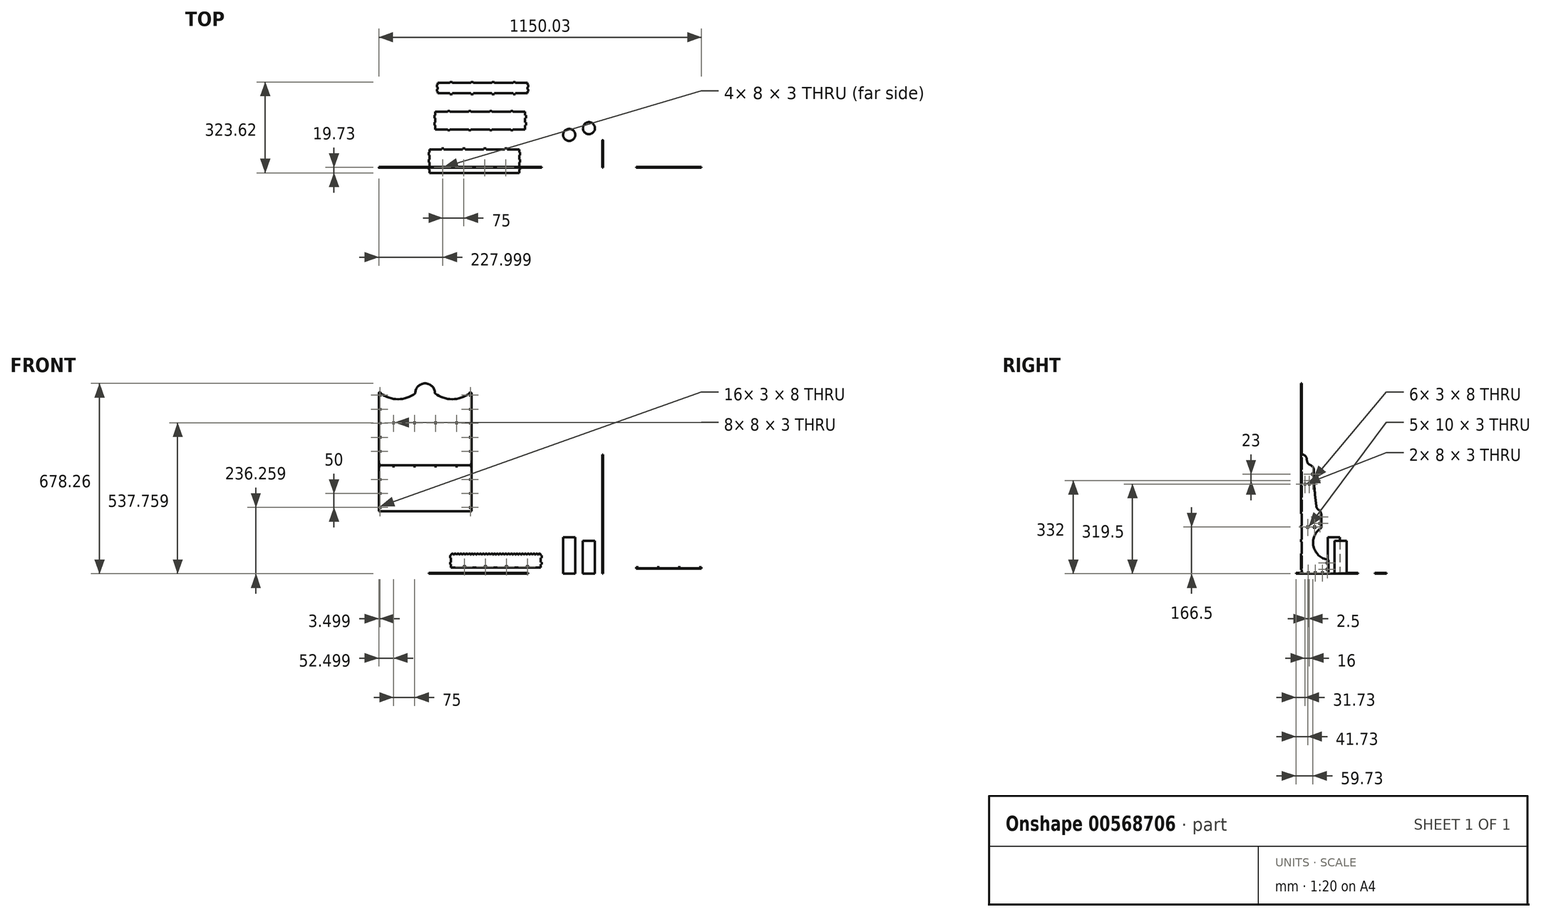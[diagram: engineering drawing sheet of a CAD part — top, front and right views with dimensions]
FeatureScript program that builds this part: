
annotation { "Feature Type Name" : "Feature", "Feature Type Description" : "" }
export const myFeature = defineFeature(function(context is Context, id is Id, definition is map)
    precondition{}
    {
        {
            var Q0;
            Q0=qCreatedBy(makeId("Right.planeOp"),FACE);
            var sketch = newSketch(context, id + "F0", { "sketchPlane" : qUnion([Q0])});
            skLineSegment(sketch, "E0", {"start": v(0, 5) * mm, "end": v(0, 14) * mm});
            skLineSegment(sketch, "E1", {"start": v(5, 0) * mm, "end": v(95, 0) * mm});
            skLineSegment(sketch, "E2", {"start": v(43, 355.36) * mm, "end": v(43, 369.6) * mm});
            skPoint(sketch, "E3", {"position": v(43, 366) * mm});
            skArc(sketch, "E4", {"start": v(5, 0) * mm, "mid": v(3.54, 3.54) * mm, "end": v(0, 5) * mm});
            skLineSegment(sketch, "E5", {"start": v(30.5, 318) * mm, "end": v(22.5, 318) * mm});
            skLineSegment(sketch, "E6", {"start": v(30.5, 321) * mm, "end": v(22.5, 321) * mm});
            skLineSegment(sketch, "E7", {"start": v(37, 359) * mm, "end": v(37, 351) * mm});
            skLineSegment(sketch, "E8", {"start": v(40, 359) * mm, "end": v(40, 351) * mm});
            skPoint(sketch, "E9", {"position": v(0, 474) * mm});
            skPoint(sketch, "E10", {"position": v(37, 359) * mm});
            skPoint(sketch, "E11", {"position": v(37, 351) * mm});
            skPoint(sketch, "E12", {"position": v(37, 336) * mm});
            skPoint(sketch, "E13", {"position": v(37, 328) * mm});
            skLineSegment(sketch, "E14", {"start": v(37, 328) * mm, "end": v(40, 328) * mm});
            skLineSegment(sketch, "E15", {"start": v(37, 336) * mm, "end": v(40, 336) * mm});
            skLineSegment(sketch, "E16", {"start": v(37, 351) * mm, "end": v(40, 351) * mm});
            skLineSegment(sketch, "E17", {"start": v(37, 359) * mm, "end": v(40, 359) * mm});
            skArc(sketch, "E18.trimOffspring", {"start": v(43, 369.6) * mm, "mid": v(38.58, 380.98) * mm, "end": v(28.7, 388.14) * mm});
            skPoint(sketch, "E19.visualSharp", {"position": v(21.6, 389.37) * mm});
            skArc(sketch, "E19.filletArc", {"start": v(18.91, 399.73) * mm, "mid": v(22.23, 392.6) * mm, "end": v(28.7, 388.14) * mm});
            skLineSegment(sketch, "E20.trimOffspring", {"start": v(40, 336) * mm, "end": v(40, 328) * mm});
            skLineSegment(sketch, "E21.trimOffspring", {"start": v(37, 336) * mm, "end": v(37, 328) * mm});
            skLineSegment(sketch, "E22.left", {"start": v(6.5, 321) * mm, "end": v(6.5, 318) * mm});
            skLineSegment(sketch, "E22.right", {"start": v(14.5, 321) * mm, "end": v(14.5, 318) * mm});
            skLineSegment(sketch, "E23.left", {"start": v(22.5, 321) * mm, "end": v(22.5, 318) * mm});
            skLineSegment(sketch, "E23.right", {"start": v(30.5, 321) * mm, "end": v(30.5, 318) * mm});
            skLineSegment(sketch, "E24.trimOffspring", {"start": v(14.5, 321) * mm, "end": v(6.5, 321) * mm});
            skLineSegment(sketch, "E25.trimOffspring", {"start": v(14.5, 318) * mm, "end": v(6.5, 318) * mm});
            skLineSegment(sketch, "E26", {"start": v(43, 318) * mm, "end": v(44, 318) * mm});
            skLineSegment(sketch, "E27.bottom", {"start": v(63, 206) * mm, "end": v(66, 206) * mm});
            skLineSegment(sketch, "E27.top", {"start": v(63, 198) * mm, "end": v(66, 198) * mm});
            skLineSegment(sketch, "E27.left", {"start": v(63, 206) * mm, "end": v(63, 198) * mm});
            skLineSegment(sketch, "E27.right", {"start": v(66, 206) * mm, "end": v(66, 198) * mm});
            skLineSegment(sketch, "E28.bottom", {"start": v(63, 183) * mm, "end": v(66, 183) * mm});
            skLineSegment(sketch, "E28.top", {"start": v(63, 175) * mm, "end": v(66, 175) * mm});
            skLineSegment(sketch, "E28.left", {"start": v(63, 183) * mm, "end": v(63, 175) * mm});
            skLineSegment(sketch, "E28.right", {"start": v(66, 183) * mm, "end": v(66, 175) * mm});
            skLineSegment(sketch, "E29.bottom", {"start": v(40.5, 165) * mm, "end": v(40.5, 168) * mm});
            skLineSegment(sketch, "E29.top", {"start": v(50.5, 165) * mm, "end": v(50.5, 168) * mm});
            skLineSegment(sketch, "E29.left", {"start": v(40.5, 165) * mm, "end": v(50.5, 165) * mm});
            skLineSegment(sketch, "E29.right", {"start": v(40.5, 168) * mm, "end": v(50.5, 168) * mm});
            skLineSegment(sketch, "E30.bottom", {"start": v(15.5, 165) * mm, "end": v(15.5, 168) * mm});
            skLineSegment(sketch, "E30.top", {"start": v(25.5, 165) * mm, "end": v(25.5, 168) * mm});
            skLineSegment(sketch, "E30.left", {"start": v(15.5, 165) * mm, "end": v(25.5, 165) * mm});
            skLineSegment(sketch, "E30.right", {"start": v(15.5, 168) * mm, "end": v(25.5, 168) * mm});
            skArc(sketch, "E31", {"start": v(69, 213) * mm, "mid": v(66.39, 220.9) * mm, "end": v(60.51, 226.8) * mm});
            skLineSegment(sketch, "E32", {"start": v(46.98, 280.85) * mm, "end": v(51.17, 241.67) * mm});
            skPoint(sketch, "E33.visualSharp", {"position": v(43, 318) * mm});
            skArc(sketch, "E33.filletArc", {"start": v(43, 355.36) * mm, "mid": v(44, 318.05) * mm, "end": v(46.98, 280.85) * mm});
            skArc(sketch, "E34.filletArc", {"start": v(51.17, 241.67) * mm, "mid": v(54.12, 233.15) * mm, "end": v(60.51, 226.8) * mm});
            skArc(sketch, "E35", {"start": v(17.5, 407.94) * mm, "mid": v(12.22, 420.03) * mm, "end": v(0, 425) * mm});
            skLineSegment(sketch, "E36", {"start": v(18.91, 399.73) * mm, "end": v(17.5, 407.94) * mm});
            skLineSegment(sketch, "E37.trimOffspring", {"start": v(0, 474) * mm, "end": v(0, 481) * mm});
            skLineSegment(sketch, "E38.bottom", {"start": v(89, 43) * mm, "end": v(92, 43) * mm});
            skLineSegment(sketch, "E38.top", {"start": v(89, 35) * mm, "end": v(92, 35) * mm});
            skLineSegment(sketch, "E38.left", {"start": v(89, 43) * mm, "end": v(89, 35) * mm});
            skLineSegment(sketch, "E38.right", {"start": v(92, 43) * mm, "end": v(92, 35) * mm});
            skLineSegment(sketch, "E39.bottom", {"start": v(92, 20) * mm, "end": v(89, 20) * mm});
            skLineSegment(sketch, "E39.top", {"start": v(92, 12) * mm, "end": v(89, 12) * mm});
            skLineSegment(sketch, "E39.left", {"start": v(92, 20) * mm, "end": v(92, 12) * mm});
            skLineSegment(sketch, "E39.right", {"start": v(89, 20) * mm, "end": v(89, 12) * mm});
            skLineSegment(sketch, "E40", {"start": v(0, 14) * mm, "end": v(-3, 14) * mm});
            skLineSegment(sketch, "E41", {"start": v(-3, 14) * mm, "end": v(-3, 22) * mm});
            skLineSegment(sketch, "E42", {"start": v(-3, 22) * mm, "end": v(0, 22) * mm});
            skLineSegment(sketch, "E43.0.1.0", {"start": v(-3, 72) * mm, "end": v(0, 72) * mm});
            skLineSegment(sketch, "E43.0.1.1", {"start": v(-3, 64) * mm, "end": v(-3, 72) * mm});
            skLineSegment(sketch, "E43.0.1.2", {"start": v(0, 64) * mm, "end": v(-3, 64) * mm});
            skLineSegment(sketch, "E43.0.2.0", {"start": v(-3, 122) * mm, "end": v(0, 122) * mm});
            skLineSegment(sketch, "E43.0.2.1", {"start": v(-3, 114) * mm, "end": v(-3, 122) * mm});
            skLineSegment(sketch, "E43.0.2.2", {"start": v(0, 114) * mm, "end": v(-3, 114) * mm});
            skLineSegment(sketch, "E43.0.3.0", {"start": v(-3, 172) * mm, "end": v(0, 172) * mm});
            skLineSegment(sketch, "E43.0.3.1", {"start": v(-3, 164) * mm, "end": v(-3, 172) * mm});
            skLineSegment(sketch, "E43.0.3.2", {"start": v(0, 164) * mm, "end": v(-3, 164) * mm});
            skLineSegment(sketch, "E43.0.4.0", {"start": v(-3, 222) * mm, "end": v(0, 222) * mm});
            skLineSegment(sketch, "E43.0.4.1", {"start": v(-3, 214) * mm, "end": v(-3, 222) * mm});
            skLineSegment(sketch, "E43.0.4.2", {"start": v(0, 214) * mm, "end": v(-3, 214) * mm});
            skLineSegment(sketch, "E43.0.5.0", {"start": v(-3, 272) * mm, "end": v(0, 272) * mm});
            skLineSegment(sketch, "E43.0.5.1", {"start": v(-3, 264) * mm, "end": v(-3, 272) * mm});
            skLineSegment(sketch, "E43.0.5.2", {"start": v(0, 264) * mm, "end": v(-3, 264) * mm});
            skLineSegment(sketch, "E43.0.6.0", {"start": v(-3, 322) * mm, "end": v(0, 322) * mm});
            skLineSegment(sketch, "E43.0.6.1", {"start": v(-3, 314) * mm, "end": v(-3, 322) * mm});
            skLineSegment(sketch, "E43.0.6.2", {"start": v(0, 314) * mm, "end": v(-3, 314) * mm});
            skLineSegment(sketch, "E43.0.7.0", {"start": v(-3, 372) * mm, "end": v(0, 372) * mm});
            skLineSegment(sketch, "E43.0.7.1", {"start": v(-3, 364) * mm, "end": v(-3, 372) * mm});
            skLineSegment(sketch, "E43.0.7.2", {"start": v(0, 364) * mm, "end": v(-3, 364) * mm});
            skLineSegment(sketch, "E43.0.8.0", {"start": v(-3, 422) * mm, "end": v(0, 422) * mm});
            skLineSegment(sketch, "E43.0.8.1", {"start": v(-3, 414) * mm, "end": v(-3, 422) * mm});
            skLineSegment(sketch, "E43.0.8.2", {"start": v(0, 414) * mm, "end": v(-3, 414) * mm});
            skLineSegment(sketch, "E43.direction1", {"start": v(-3, 22) * mm, "end": v(22, 22) * mm, "construction": true});
            skLineSegment(sketch, "E43.direction2", {"start": v(-3, 22) * mm, "end": v(-3, 72) * mm, "construction": true});
            skLineSegment(sketch, "E44.bottom", {"start": v(43, 2) * mm, "end": v(43, 5) * mm});
            skLineSegment(sketch, "E44.top", {"start": v(53, 2) * mm, "end": v(53, 5) * mm});
            skLineSegment(sketch, "E44.right", {"start": v(43, 5) * mm, "end": v(53, 5) * mm});
            skLineSegment(sketch, "E45.bottom", {"start": v(18, 2) * mm, "end": v(18, 5) * mm});
            skLineSegment(sketch, "E45.top", {"start": v(28, 2) * mm, "end": v(28, 5) * mm});
            skLineSegment(sketch, "E45.right", {"start": v(18, 5) * mm, "end": v(28, 5) * mm});
            skLineSegment(sketch, "E46.bottom", {"start": v(68, 2) * mm, "end": v(68, 5) * mm});
            skLineSegment(sketch, "E46.top", {"start": v(78, 2) * mm, "end": v(78, 5) * mm});
            skLineSegment(sketch, "E46.right", {"start": v(68, 5) * mm, "end": v(78, 5) * mm});
            skLineSegment(sketch, "E47", {"start": v(18, 2) * mm, "end": v(28, 2) * mm});
            skLineSegment(sketch, "E48", {"start": v(43, 2) * mm, "end": v(53, 2) * mm});
            skLineSegment(sketch, "E49", {"start": v(68, 2) * mm, "end": v(78, 2) * mm});
            skPoint(sketch, "E50.end.orphan", {"position": v(89, 165) * mm});
            skPoint(sketch, "E51.visualSharp", {"position": v(95, 50) * mm});
            skPoint(sketch, "E52.visualSharp", {"position": v(69, 165) * mm});
            skLineSegment(sketch, "E53.trimOffspring", {"start": v(0, 422) * mm, "end": v(0, 425) * mm});
            skLineSegment(sketch, "E54.trimOffspring", {"start": v(0, 372) * mm, "end": v(0, 414) * mm});
            skLineSegment(sketch, "E55.trimOffspring", {"start": v(0, 322) * mm, "end": v(0, 364) * mm});
            skLineSegment(sketch, "E56.trimOffspring", {"start": v(0, 272) * mm, "end": v(0, 314) * mm});
            skLineSegment(sketch, "E57.trimOffspring", {"start": v(0, 222) * mm, "end": v(0, 264) * mm});
            skLineSegment(sketch, "E58.trimOffspring", {"start": v(0, 172) * mm, "end": v(0, 214) * mm});
            skLineSegment(sketch, "E59.trimOffspring", {"start": v(0, 122) * mm, "end": v(0, 164) * mm});
            skLineSegment(sketch, "E60.trimOffspring", {"start": v(0, 72) * mm, "end": v(0, 114) * mm});
            skLineSegment(sketch, "E61.trimOffspring", {"start": v(0, 22) * mm, "end": v(0, 64) * mm});
            skArc(sketch, "E62", {"start": v(66.82, 161.58) * mm, "mid": v(41.64, 97.2) * mm, "end": v(92.44, 50.32) * mm});
            skLineSegment(sketch, "E63", {"start": v(69, 213) * mm, "end": v(69, 165.7) * mm});
            skLineSegment(sketch, "E64", {"start": v(95, 0) * mm, "end": v(95, 47.35) * mm});
            skArc(sketch, "E65.filletArc", {"start": v(95, 47.35) * mm, "mid": v(94.27, 49.32) * mm, "end": v(92.44, 50.32) * mm});
            skPoint(sketch, "E66.visualSharp", {"position": v(69, 163) * mm});
            skArc(sketch, "E66.filletArc", {"start": v(66.82, 161.58) * mm, "mid": v(68.42, 163.37) * mm, "end": v(69, 165.7) * mm});
            skSolve(sketch);
        }
        {
            var Q0;
            Q0=makeQuery(id+"F0.imprint","IMPRINT",FACE,{"disambiguationData":[TD([[makeQuery(id+"F0.imprint","IMPRINT",EDGE,{"derivedFrom":sQuery(id+"F0.wireOp",EDGE,"E0")}),-1.0]])]});
            extrude(context, id + "F1", {"entities" : qUnion([Q0]), "depth" : 3 * mm, "offsetDistance" : 25 * mm});
        }
        {
            var Q0;
            Q0=qCreatedBy(makeId("Top.planeOp"),FACE);
            var sketch = newSketch(context, id + "F2", { "sketchPlane" : qUnion([Q0])});
            skLineSegment(sketch, "E67.bottom", {"start": v(-615.77, -21.23) * mm, "end": v(-295.77, -21.23) * mm});
            skLineSegment(sketch, "E67.top", {"start": v(-615.77, 62.77) * mm, "end": v(-572.27, 62.77) * mm});
            skLineSegment(sketch, "E67.left", {"start": v(-615.77, -21.23) * mm, "end": v(-615.77, -8.23) * mm});
            skLineSegment(sketch, "E67.right", {"start": v(-295.77, -21.23) * mm, "end": v(-295.77, -8.23) * mm});
            skLineSegment(sketch, "E68", {"start": v(-339.27, 62.77) * mm, "end": v(-339.27, 65.77) * mm});
            skLineSegment(sketch, "E69", {"start": v(-347.27, 65.77) * mm, "end": v(-347.27, 62.77) * mm});
            skLineSegment(sketch, "E70.1.0.0", {"start": v(-422.27, 65.77) * mm, "end": v(-422.27, 62.77) * mm});
            skLineSegment(sketch, "E70.1.0.1", {"start": v(-414.27, 62.77) * mm, "end": v(-414.27, 65.77) * mm});
            skLineSegment(sketch, "E70.2.0.0", {"start": v(-497.27, 65.77) * mm, "end": v(-497.27, 62.77) * mm});
            skLineSegment(sketch, "E70.2.0.1", {"start": v(-489.27, 62.77) * mm, "end": v(-489.27, 65.77) * mm});
            skLineSegment(sketch, "E70.3.0.0", {"start": v(-572.27, 65.77) * mm, "end": v(-572.27, 62.77) * mm});
            skLineSegment(sketch, "E70.3.0.1", {"start": v(-564.27, 62.77) * mm, "end": v(-564.27, 65.77) * mm});
            skLineSegment(sketch, "E70.direction1", {"start": v(-347.27, 62.77) * mm, "end": v(-414.27, 62.77) * mm, "construction": true});
            skLineSegment(sketch, "E71", {"start": v(-572.27, 65.77) * mm, "end": v(-564.27, 65.77) * mm});
            skLineSegment(sketch, "E72", {"start": v(-497.27, 65.77) * mm, "end": v(-489.27, 65.77) * mm});
            skLineSegment(sketch, "E73", {"start": v(-422.27, 65.77) * mm, "end": v(-414.27, 65.77) * mm});
            skLineSegment(sketch, "E74", {"start": v(-347.27, 65.77) * mm, "end": v(-339.27, 65.77) * mm});
            skLineSegment(sketch, "E75.trimOffspring", {"start": v(-564.27, 62.77) * mm, "end": v(-497.27, 62.77) * mm});
            skLineSegment(sketch, "E76.trimOffspring", {"start": v(-489.27, 62.77) * mm, "end": v(-422.27, 62.77) * mm});
            skLineSegment(sketch, "E77.trimOffspring", {"start": v(-339.27, 62.77) * mm, "end": v(-295.77, 62.77) * mm});
            skLineSegment(sketch, "E78.trimOffspring", {"start": v(-414.27, 62.77) * mm, "end": v(-347.27, 62.77) * mm});
            skLineSegment(sketch, "E79.3.0.0", {"start": v(-295.77, 41.77) * mm, "end": v(-292.77, 41.77) * mm});
            skLineSegment(sketch, "E79.3.0.1", {"start": v(-292.77, 51.77) * mm, "end": v(-295.77, 51.77) * mm});
            skLineSegment(sketch, "E80.0.1.0", {"start": v(-292.77, 26.77) * mm, "end": v(-295.77, 26.77) * mm});
            skLineSegment(sketch, "E80.0.1.1", {"start": v(-295.77, 16.77) * mm, "end": v(-292.77, 16.77) * mm});
            skLineSegment(sketch, "E80.0.2.0", {"start": v(-292.77, 1.77) * mm, "end": v(-295.77, 1.77) * mm});
            skLineSegment(sketch, "E80.0.2.1", {"start": v(-295.77, -8.23) * mm, "end": v(-292.77, -8.23) * mm});
            skLineSegment(sketch, "E80.1.0.0", {"start": v(-615.77, 51.77) * mm, "end": v(-618.77, 51.77) * mm});
            skLineSegment(sketch, "E80.1.0.1", {"start": v(-618.77, 41.77) * mm, "end": v(-615.77, 41.77) * mm});
            skLineSegment(sketch, "E80.1.1.0", {"start": v(-615.77, 26.77) * mm, "end": v(-618.77, 26.77) * mm});
            skLineSegment(sketch, "E80.1.1.1", {"start": v(-618.77, 16.77) * mm, "end": v(-615.77, 16.77) * mm});
            skLineSegment(sketch, "E80.1.2.0", {"start": v(-615.77, 1.77) * mm, "end": v(-618.77, 1.77) * mm});
            skLineSegment(sketch, "E80.1.2.1", {"start": v(-618.77, -8.23) * mm, "end": v(-615.77, -8.23) * mm});
            skLineSegment(sketch, "E80.direction1", {"start": v(-295.77, 51.77) * mm, "end": v(-618.77, 51.77) * mm, "construction": true});
            skLineSegment(sketch, "E80.direction2", {"start": v(-295.77, 41.77) * mm, "end": v(-295.77, 26.77) * mm, "construction": true});
            skLineSegment(sketch, "E81", {"start": v(-618.77, 51.77) * mm, "end": v(-618.77, 41.77) * mm});
            skLineSegment(sketch, "E82", {"start": v(-618.77, 26.77) * mm, "end": v(-618.77, 16.77) * mm});
            skLineSegment(sketch, "E83", {"start": v(-618.77, 1.77) * mm, "end": v(-618.77, -8.23) * mm});
            skLineSegment(sketch, "E84", {"start": v(-292.77, -8.23) * mm, "end": v(-292.77, 1.77) * mm});
            skLineSegment(sketch, "E85", {"start": v(-292.77, 16.77) * mm, "end": v(-292.77, 26.77) * mm});
            skLineSegment(sketch, "E86", {"start": v(-292.77, 41.77) * mm, "end": v(-292.77, 51.77) * mm});
            skLineSegment(sketch, "E87.trimOffspring", {"start": v(-615.77, 1.77) * mm, "end": v(-615.77, 16.77) * mm});
            skLineSegment(sketch, "E88.trimOffspring", {"start": v(-615.77, 26.77) * mm, "end": v(-615.77, 41.77) * mm});
            skLineSegment(sketch, "E89.trimOffspring", {"start": v(-615.77, 51.77) * mm, "end": v(-615.77, 62.77) * mm});
            skLineSegment(sketch, "E90.trimOffspring", {"start": v(-295.77, 1.77) * mm, "end": v(-295.77, 16.77) * mm});
            skLineSegment(sketch, "E91.trimOffspring", {"start": v(-295.77, 26.77) * mm, "end": v(-295.77, 41.77) * mm});
            skLineSegment(sketch, "E92.trimOffspring", {"start": v(-295.77, 51.77) * mm, "end": v(-295.77, 62.77) * mm});
            skLineSegment(sketch, "E93.bottom", {"start": v(-572.27, -3) * mm, "end": v(-564.27, -3) * mm});
            skLineSegment(sketch, "E93.top", {"start": v(-572.27, 0) * mm, "end": v(-564.27, 0) * mm});
            skLineSegment(sketch, "E93.left", {"start": v(-572.27, -3) * mm, "end": v(-572.27, 0) * mm});
            skLineSegment(sketch, "E93.right", {"start": v(-564.27, -3) * mm, "end": v(-564.27, 0) * mm});
            skLineSegment(sketch, "E94.1.0.0", {"start": v(-497.27, 0) * mm, "end": v(-489.27, 0) * mm});
            skLineSegment(sketch, "E94.1.0.1", {"start": v(-489.27, -3) * mm, "end": v(-489.27, 0) * mm});
            skLineSegment(sketch, "E94.1.0.2", {"start": v(-497.27, -3) * mm, "end": v(-489.27, -3) * mm});
            skLineSegment(sketch, "E94.1.0.3", {"start": v(-497.27, -3) * mm, "end": v(-497.27, 0) * mm});
            skLineSegment(sketch, "E94.2.0.0", {"start": v(-422.27, 0) * mm, "end": v(-414.27, 0) * mm});
            skLineSegment(sketch, "E94.2.0.1", {"start": v(-414.27, -3) * mm, "end": v(-414.27, 0) * mm});
            skLineSegment(sketch, "E94.2.0.2", {"start": v(-422.27, -3) * mm, "end": v(-414.27, -3) * mm});
            skLineSegment(sketch, "E94.2.0.3", {"start": v(-422.27, -3) * mm, "end": v(-422.27, 0) * mm});
            skLineSegment(sketch, "E94.3.0.0", {"start": v(-347.27, 0) * mm, "end": v(-339.27, 0) * mm});
            skLineSegment(sketch, "E94.3.0.1", {"start": v(-339.27, -3) * mm, "end": v(-339.27, 0) * mm});
            skLineSegment(sketch, "E94.3.0.2", {"start": v(-347.27, -3) * mm, "end": v(-339.27, -3) * mm});
            skLineSegment(sketch, "E94.3.0.3", {"start": v(-347.27, -3) * mm, "end": v(-347.27, 0) * mm});
            skLineSegment(sketch, "E94.direction1", {"start": v(-572.27, 0) * mm, "end": v(-497.27, 0) * mm, "construction": true});
            skSolve(sketch);
        }
        {
            var Q0;
            Q0=makeQuery(id+"F2.imprint","IMPRINT",FACE,{"disambiguationData":[TD([[makeQuery(id+"F2.imprint","IMPRINT",EDGE,{"derivedFrom":sQuery(id+"F2.wireOp",EDGE,"E67.bottom")}),1.0]])]});
            extrude(context, id + "F3", {"entities" : qUnion([Q0]), "depth" : 3 * mm, "offsetDistance" : 25 * mm});
        }
        {
            var Q0;
            Q0=qCreatedBy(makeId("Front.planeOp"),FACE);
            var sketch = newSketch(context, id + "F4", { "sketchPlane" : qUnion([Q0])});
            skLineSegment(sketch, "E95.left", {"start": v(-218.83, 22.74) * mm, "end": v(-218.83, 33.74) * mm});
            skLineSegment(sketch, "E95.right", {"start": v(-538.83, 22.74) * mm, "end": v(-538.83, 33.74) * mm});
            skLineSegment(sketch, "E96.3.0.0", {"start": v(-218.83, 56.74) * mm, "end": v(-215.83, 56.74) * mm});
            skLineSegment(sketch, "E96.3.0.1", {"start": v(-215.83, 64.74) * mm, "end": v(-218.83, 64.74) * mm});
            skLineSegment(sketch, "E97.0.1.0", {"start": v(-215.83, 41.74) * mm, "end": v(-218.83, 41.74) * mm});
            skLineSegment(sketch, "E97.0.1.1", {"start": v(-218.83, 33.74) * mm, "end": v(-215.83, 33.74) * mm});
            skLineSegment(sketch, "E97.1.0.0", {"start": v(-538.83, 64.74) * mm, "end": v(-541.83, 64.74) * mm});
            skLineSegment(sketch, "E97.1.0.1", {"start": v(-541.83, 56.74) * mm, "end": v(-538.83, 56.74) * mm});
            skLineSegment(sketch, "E97.1.1.0", {"start": v(-538.83, 41.74) * mm, "end": v(-541.83, 41.74) * mm});
            skLineSegment(sketch, "E97.1.1.1", {"start": v(-541.83, 33.74) * mm, "end": v(-538.83, 33.74) * mm});
            skLineSegment(sketch, "E97.direction1", {"start": v(-218.83, 64.74) * mm, "end": v(-541.83, 64.74) * mm, "construction": true});
            skLineSegment(sketch, "E97.direction2", {"start": v(-218.83, 56.74) * mm, "end": v(-218.83, 41.74) * mm, "construction": true});
            skLineSegment(sketch, "E98.bottom", {"start": v(-262.33, 23.74) * mm, "end": v(-270.33, 23.74) * mm});
            skLineSegment(sketch, "E98.top", {"start": v(-262.33, 26.74) * mm, "end": v(-270.33, 26.74) * mm});
            skLineSegment(sketch, "E98.left", {"start": v(-262.33, 23.74) * mm, "end": v(-262.33, 26.74) * mm});
            skLineSegment(sketch, "E98.right", {"start": v(-270.33, 23.74) * mm, "end": v(-270.33, 26.74) * mm});
            skLineSegment(sketch, "E99.1.0.0", {"start": v(-337.33, 23.74) * mm, "end": v(-337.33, 26.74) * mm});
            skLineSegment(sketch, "E99.1.0.1", {"start": v(-337.33, 26.74) * mm, "end": v(-345.33, 26.74) * mm});
            skLineSegment(sketch, "E99.1.0.2", {"start": v(-337.33, 23.74) * mm, "end": v(-345.33, 23.74) * mm});
            skLineSegment(sketch, "E99.1.0.3", {"start": v(-345.33, 23.74) * mm, "end": v(-345.33, 26.74) * mm});
            skLineSegment(sketch, "E99.direction1", {"start": v(-262.33, 23.74) * mm, "end": v(-337.33, 23.74) * mm, "construction": true});
            skLineSegment(sketch, "E100", {"start": v(-215.83, 64.74) * mm, "end": v(-215.83, 56.74) * mm});
            skLineSegment(sketch, "E101", {"start": v(-215.83, 41.74) * mm, "end": v(-215.83, 33.74) * mm});
            skLineSegment(sketch, "E102", {"start": v(-541.83, 64.74) * mm, "end": v(-541.83, 56.74) * mm});
            skLineSegment(sketch, "E103", {"start": v(-541.83, 41.74) * mm, "end": v(-541.83, 33.74) * mm});
            skLineSegment(sketch, "E104.trimOffspring", {"start": v(-218.83, 41.74) * mm, "end": v(-218.83, 56.74) * mm});
            skLineSegment(sketch, "E105.trimOffspring", {"start": v(-218.83, 64.74) * mm, "end": v(-218.83, 66.74) * mm});
            skLineSegment(sketch, "E106.trimOffspring", {"start": v(-538.83, 64.74) * mm, "end": v(-538.83, 66.74) * mm});
            skLineSegment(sketch, "E107.trimOffspring", {"start": v(-538.83, 41.74) * mm, "end": v(-538.83, 56.74) * mm});
            skLineSegment(sketch, "E108.0.2.0", {"start": v(-412.33, 23.74) * mm, "end": v(-412.33, 26.74) * mm});
            skLineSegment(sketch, "E108.3.2.0", {"start": v(-412.33, 26.74) * mm, "end": v(-420.33, 26.74) * mm});
            skLineSegment(sketch, "E108.6.2.0", {"start": v(-412.33, 23.74) * mm, "end": v(-420.33, 23.74) * mm});
            skLineSegment(sketch, "E108.9.2.0", {"start": v(-420.33, 23.74) * mm, "end": v(-420.33, 26.74) * mm});
            skLineSegment(sketch, "E108.0.3.0", {"start": v(-487.33, 23.74) * mm, "end": v(-487.33, 26.74) * mm});
            skLineSegment(sketch, "E108.3.3.0", {"start": v(-487.33, 26.74) * mm, "end": v(-495.33, 26.74) * mm});
            skLineSegment(sketch, "E108.6.3.0", {"start": v(-487.33, 23.74) * mm, "end": v(-495.33, 23.74) * mm});
            skLineSegment(sketch, "E108.9.3.0", {"start": v(-495.33, 23.74) * mm, "end": v(-495.33, 26.74) * mm});
            skPoint(sketch, "E109", {"position": v(-218.83, 66.74) * mm});
            skArc(sketch, "E110", {"start": v(-218.83, 66.74) * mm, "mid": v(-223.83, 71.74) * mm, "end": v(-228.83, 66.74) * mm});
            skPoint(sketch, "E111.orphan", {"position": v(-218.83, 71.74) * mm});
            skArc(sketch, "E112.1.0.0", {"start": v(-228.83, 66.74) * mm, "mid": v(-233.83, 71.74) * mm, "end": v(-238.83, 66.74) * mm});
            skArc(sketch, "E112.2.0.0", {"start": v(-238.83, 66.74) * mm, "mid": v(-243.83, 71.74) * mm, "end": v(-248.83, 66.74) * mm});
            skArc(sketch, "E112.3.0.0", {"start": v(-248.83, 66.74) * mm, "mid": v(-253.83, 71.74) * mm, "end": v(-258.83, 66.74) * mm});
            skArc(sketch, "E112.4.0.0", {"start": v(-258.83, 66.74) * mm, "mid": v(-263.83, 71.74) * mm, "end": v(-268.83, 66.74) * mm});
            skArc(sketch, "E112.5.0.0", {"start": v(-268.83, 66.74) * mm, "mid": v(-273.83, 71.74) * mm, "end": v(-278.83, 66.74) * mm});
            skArc(sketch, "E112.6.0.0", {"start": v(-278.83, 66.74) * mm, "mid": v(-283.83, 71.74) * mm, "end": v(-288.83, 66.74) * mm});
            skArc(sketch, "E112.7.0.0", {"start": v(-288.83, 66.74) * mm, "mid": v(-293.83, 71.74) * mm, "end": v(-298.83, 66.74) * mm});
            skArc(sketch, "E112.8.0.0", {"start": v(-298.83, 66.74) * mm, "mid": v(-303.83, 71.74) * mm, "end": v(-308.83, 66.74) * mm});
            skArc(sketch, "E112.9.0.0", {"start": v(-308.83, 66.74) * mm, "mid": v(-313.83, 71.74) * mm, "end": v(-318.83, 66.74) * mm});
            skArc(sketch, "E112.10.0.0", {"start": v(-318.83, 66.74) * mm, "mid": v(-323.83, 71.74) * mm, "end": v(-328.83, 66.74) * mm});
            skArc(sketch, "E112.11.0.0", {"start": v(-328.83, 66.74) * mm, "mid": v(-333.83, 71.74) * mm, "end": v(-338.83, 66.74) * mm});
            skArc(sketch, "E112.12.0.0", {"start": v(-338.83, 66.74) * mm, "mid": v(-343.83, 71.74) * mm, "end": v(-348.83, 66.74) * mm});
            skArc(sketch, "E112.13.0.0", {"start": v(-348.83, 66.74) * mm, "mid": v(-353.83, 71.74) * mm, "end": v(-358.83, 66.74) * mm});
            skArc(sketch, "E112.14.0.0", {"start": v(-358.83, 66.74) * mm, "mid": v(-363.83, 71.74) * mm, "end": v(-368.83, 66.74) * mm});
            skArc(sketch, "E112.15.0.0", {"start": v(-368.83, 66.74) * mm, "mid": v(-373.83, 71.74) * mm, "end": v(-378.83, 66.74) * mm});
            skArc(sketch, "E112.16.0.0", {"start": v(-378.83, 66.74) * mm, "mid": v(-383.83, 71.74) * mm, "end": v(-388.83, 66.74) * mm});
            skArc(sketch, "E112.17.0.0", {"start": v(-388.83, 66.74) * mm, "mid": v(-393.83, 71.74) * mm, "end": v(-398.83, 66.74) * mm});
            skArc(sketch, "E112.18.0.0", {"start": v(-398.83, 66.74) * mm, "mid": v(-403.83, 71.74) * mm, "end": v(-408.83, 66.74) * mm});
            skArc(sketch, "E112.19.0.0", {"start": v(-408.83, 66.74) * mm, "mid": v(-413.83, 71.74) * mm, "end": v(-418.83, 66.74) * mm});
            skArc(sketch, "E112.20.0.0", {"start": v(-418.83, 66.74) * mm, "mid": v(-423.83, 71.74) * mm, "end": v(-428.83, 66.74) * mm});
            skArc(sketch, "E112.21.0.0", {"start": v(-428.83, 66.74) * mm, "mid": v(-433.83, 71.74) * mm, "end": v(-438.83, 66.74) * mm});
            skArc(sketch, "E112.22.0.0", {"start": v(-438.83, 66.74) * mm, "mid": v(-443.83, 71.74) * mm, "end": v(-448.83, 66.74) * mm});
            skArc(sketch, "E112.23.0.0", {"start": v(-448.83, 66.74) * mm, "mid": v(-453.83, 71.74) * mm, "end": v(-458.83, 66.74) * mm});
            skArc(sketch, "E112.24.0.0", {"start": v(-458.83, 66.74) * mm, "mid": v(-463.83, 71.74) * mm, "end": v(-468.83, 66.74) * mm});
            skArc(sketch, "E112.25.0.0", {"start": v(-468.83, 66.74) * mm, "mid": v(-473.83, 71.74) * mm, "end": v(-478.83, 66.74) * mm});
            skArc(sketch, "E112.26.0.0", {"start": v(-478.83, 66.74) * mm, "mid": v(-483.83, 71.74) * mm, "end": v(-488.83, 66.74) * mm});
            skArc(sketch, "E112.27.0.0", {"start": v(-488.83, 66.74) * mm, "mid": v(-493.83, 71.74) * mm, "end": v(-498.83, 66.74) * mm});
            skArc(sketch, "E112.28.0.0", {"start": v(-498.83, 66.74) * mm, "mid": v(-503.83, 71.74) * mm, "end": v(-508.83, 66.74) * mm});
            skArc(sketch, "E112.29.0.0", {"start": v(-508.83, 66.74) * mm, "mid": v(-513.83, 71.74) * mm, "end": v(-518.83, 66.74) * mm});
            skArc(sketch, "E112.30.0.0", {"start": v(-518.83, 66.74) * mm, "mid": v(-523.83, 71.74) * mm, "end": v(-528.83, 66.74) * mm});
            skArc(sketch, "E112.31.0.0", {"start": v(-528.83, 66.74) * mm, "mid": v(-533.83, 71.74) * mm, "end": v(-538.83, 66.74) * mm});
            skLineSegment(sketch, "E112.direction1", {"start": v(-228.83, 66.74) * mm, "end": v(-238.83, 66.74) * mm, "construction": true});
            skPoint(sketch, "E113.orphan", {"position": v(-538.83, 71.74) * mm});
            skLineSegment(sketch, "E114", {"start": v(-538.83, 22.74) * mm, "end": v(-218.83, 22.74) * mm});
            skSolve(sketch);
        }
        {
            var Q0;
            Q0=makeQuery(id+"F4.imprint","IMPRINT",FACE,{"disambiguationData":[TD([[makeQuery(id+"F4.imprint","IMPRINT",EDGE,{"derivedFrom":sQuery(id+"F4.wireOp",EDGE,"E95.bottom")}),-1.0]])]});
            var Q1;
            Q1=makeQuery(id+"F4.imprint","IMPRINT",FACE,{"disambiguationData":[TD([[makeQuery(id+"F4.imprint","IMPRINT",EDGE,{"derivedFrom":sQuery(id+"F4.wireOp",EDGE,"E95.left")}),1.0]])]});
            extrude(context, id + "F5", {"entities" : qUnion([Q0, Q1]), "depth" : 3 * mm, "offsetDistance" : 25 * mm});
        }
        {
            var Q0;
            Q0=qCreatedBy(makeId("Top.planeOp"),FACE);
            var sketch = newSketch(context, id + "F6", { "sketchPlane" : qUnion([Q0])});
            skLineSegment(sketch, "E115.bottom", {"start": v(-594.75, 196.79) * mm, "end": v(-551.25, 196.79) * mm});
            skLineSegment(sketch, "E115.top", {"start": v(-594.75, 133.79) * mm, "end": v(-551.25, 133.79) * mm});
            skLineSegment(sketch, "E115.left", {"start": v(-594.75, 196.79) * mm, "end": v(-594.75, 184.29) * mm});
            skLineSegment(sketch, "E115.right", {"start": v(-274.75, 196.79) * mm, "end": v(-274.75, 184.29) * mm});
            skLineSegment(sketch, "E116.3.0.0", {"start": v(-274.75, 174.29) * mm, "end": v(-271.75, 174.29) * mm});
            skLineSegment(sketch, "E116.3.0.1", {"start": v(-271.75, 184.29) * mm, "end": v(-274.75, 184.29) * mm});
            skLineSegment(sketch, "E117.0.1.0", {"start": v(-271.75, 159.29) * mm, "end": v(-274.75, 159.29) * mm});
            skLineSegment(sketch, "E117.0.1.1", {"start": v(-274.75, 149.29) * mm, "end": v(-271.75, 149.29) * mm});
            skLineSegment(sketch, "E117.1.0.0", {"start": v(-594.75, 184.29) * mm, "end": v(-597.75, 184.29) * mm});
            skLineSegment(sketch, "E117.1.0.1", {"start": v(-597.75, 174.29) * mm, "end": v(-594.75, 174.29) * mm});
            skLineSegment(sketch, "E117.1.1.0", {"start": v(-594.75, 159.29) * mm, "end": v(-597.75, 159.29) * mm});
            skLineSegment(sketch, "E117.1.1.1", {"start": v(-597.75, 149.29) * mm, "end": v(-594.75, 149.29) * mm});
            skLineSegment(sketch, "E117.direction1", {"start": v(-274.75, 184.29) * mm, "end": v(-597.75, 184.29) * mm, "construction": true});
            skLineSegment(sketch, "E117.direction2", {"start": v(-274.75, 174.29) * mm, "end": v(-274.75, 159.29) * mm, "construction": true});
            skLineSegment(sketch, "E118", {"start": v(-597.75, 184.29) * mm, "end": v(-597.75, 174.29) * mm});
            skLineSegment(sketch, "E119", {"start": v(-597.75, 159.29) * mm, "end": v(-597.75, 149.29) * mm});
            skLineSegment(sketch, "E120", {"start": v(-271.75, 184.29) * mm, "end": v(-271.75, 174.29) * mm});
            skLineSegment(sketch, "E121", {"start": v(-271.75, 159.29) * mm, "end": v(-271.75, 149.29) * mm});
            skLineSegment(sketch, "E122.3.0.0", {"start": v(-489.48, 258.31) * mm, "end": v(-489.48, 255.31) * mm});
            skLineSegment(sketch, "E122.3.0.1", {"start": v(-481.48, 255.31) * mm, "end": v(-481.48, 258.31) * mm});
            skLineSegment(sketch, "E123.3.0.0", {"start": v(-326.25, 199.79) * mm, "end": v(-326.25, 196.79) * mm});
            skLineSegment(sketch, "E123.3.0.1", {"start": v(-318.25, 196.79) * mm, "end": v(-318.25, 199.79) * mm});
            skLineSegment(sketch, "E124.0.1.0", {"start": v(-318.25, 130.79) * mm, "end": v(-318.25, 133.79) * mm});
            skLineSegment(sketch, "E124.0.1.1", {"start": v(-326.25, 133.79) * mm, "end": v(-326.25, 130.79) * mm});
            skLineSegment(sketch, "E124.1.0.0", {"start": v(-393.25, 196.79) * mm, "end": v(-393.25, 199.79) * mm});
            skLineSegment(sketch, "E124.1.0.1", {"start": v(-401.25, 199.79) * mm, "end": v(-401.25, 196.79) * mm});
            skLineSegment(sketch, "E124.1.1.0", {"start": v(-393.25, 130.79) * mm, "end": v(-393.25, 133.79) * mm});
            skLineSegment(sketch, "E124.1.1.1", {"start": v(-401.25, 133.79) * mm, "end": v(-401.25, 130.79) * mm});
            skLineSegment(sketch, "E124.2.0.0", {"start": v(-468.25, 196.79) * mm, "end": v(-468.25, 199.79) * mm});
            skLineSegment(sketch, "E124.2.0.1", {"start": v(-476.25, 199.79) * mm, "end": v(-476.25, 196.79) * mm});
            skLineSegment(sketch, "E124.2.1.0", {"start": v(-468.25, 130.79) * mm, "end": v(-468.25, 133.79) * mm});
            skLineSegment(sketch, "E124.2.1.1", {"start": v(-476.25, 133.79) * mm, "end": v(-476.25, 130.79) * mm});
            skLineSegment(sketch, "E124.3.0.0", {"start": v(-543.25, 196.79) * mm, "end": v(-543.25, 199.79) * mm});
            skLineSegment(sketch, "E124.3.0.1", {"start": v(-551.25, 199.79) * mm, "end": v(-551.25, 196.79) * mm});
            skLineSegment(sketch, "E124.3.1.0", {"start": v(-543.25, 130.79) * mm, "end": v(-543.25, 133.79) * mm});
            skLineSegment(sketch, "E124.3.1.1", {"start": v(-551.25, 133.79) * mm, "end": v(-551.25, 130.79) * mm});
            skLineSegment(sketch, "E124.direction1", {"start": v(-326.25, 196.79) * mm, "end": v(-393.25, 196.79) * mm, "construction": true});
            skLineSegment(sketch, "E124.direction2", {"start": v(-318.25, 196.79) * mm, "end": v(-318.25, 130.79) * mm, "construction": true});
            skLineSegment(sketch, "E125", {"start": v(-551.25, 130.79) * mm, "end": v(-543.25, 130.79) * mm});
            skLineSegment(sketch, "E126", {"start": v(-476.25, 130.79) * mm, "end": v(-468.25, 130.79) * mm});
            skLineSegment(sketch, "E127", {"start": v(-401.25, 130.79) * mm, "end": v(-393.25, 130.79) * mm});
            skLineSegment(sketch, "E128", {"start": v(-326.25, 130.79) * mm, "end": v(-318.25, 130.79) * mm});
            skLineSegment(sketch, "E129", {"start": v(-318.25, 199.79) * mm, "end": v(-326.25, 199.79) * mm});
            skLineSegment(sketch, "E130", {"start": v(-393.25, 199.79) * mm, "end": v(-401.25, 199.79) * mm});
            skLineSegment(sketch, "E131", {"start": v(-551.25, 199.79) * mm, "end": v(-543.25, 199.79) * mm});
            skLineSegment(sketch, "E132", {"start": v(-476.25, 199.79) * mm, "end": v(-468.25, 199.79) * mm});
            skLineSegment(sketch, "E133.trimOffspring", {"start": v(-594.75, 174.29) * mm, "end": v(-594.75, 159.29) * mm});
            skLineSegment(sketch, "E134.trimOffspring", {"start": v(-594.75, 149.29) * mm, "end": v(-594.75, 133.79) * mm});
            skLineSegment(sketch, "E135.trimOffspring", {"start": v(-543.25, 196.79) * mm, "end": v(-476.25, 196.79) * mm});
            skLineSegment(sketch, "E136.trimOffspring", {"start": v(-543.25, 133.79) * mm, "end": v(-476.25, 133.79) * mm});
            skLineSegment(sketch, "E137.trimOffspring", {"start": v(-468.25, 133.79) * mm, "end": v(-401.25, 133.79) * mm});
            skLineSegment(sketch, "E138.trimOffspring", {"start": v(-468.25, 196.79) * mm, "end": v(-401.25, 196.79) * mm});
            skLineSegment(sketch, "E139.trimOffspring", {"start": v(-393.25, 196.79) * mm, "end": v(-326.25, 196.79) * mm});
            skLineSegment(sketch, "E140.trimOffspring", {"start": v(-393.25, 133.79) * mm, "end": v(-326.25, 133.79) * mm});
            skLineSegment(sketch, "E141.trimOffspring", {"start": v(-318.25, 133.79) * mm, "end": v(-274.75, 133.79) * mm});
            skLineSegment(sketch, "E142.trimOffspring", {"start": v(-318.25, 196.79) * mm, "end": v(-274.75, 196.79) * mm});
            skLineSegment(sketch, "E143.trimOffspring", {"start": v(-274.75, 149.29) * mm, "end": v(-274.75, 133.79) * mm});
            skLineSegment(sketch, "E144.trimOffspring", {"start": v(-274.75, 174.29) * mm, "end": v(-274.75, 159.29) * mm});
            skSolve(sketch);
        }
        {
            var Q0;
            Q0=makeQuery(id+"F6.imprint","IMPRINT",FACE,{"disambiguationData":[TD([[makeQuery(id+"F6.imprint","IMPRINT",EDGE,{"derivedFrom":sQuery(id+"F6.wireOp",EDGE,"E115.bottom")}),-1.0]])]});
            extrude(context, id + "F7", {"entities" : qUnion([Q0]), "depth" : 3 * mm, "offsetDistance" : 25 * mm});
        }
        {
            var Q0;
            Q0=qCreatedBy(makeId("Top.planeOp"),FACE);
            var sketch = newSketch(context, id + "F8", { "sketchPlane" : qUnion([Q0])});
            skLineSegment(sketch, "E145.bottom", {"start": v(-586.32, 299.4) * mm, "end": v(-542.82, 299.4) * mm});
            skLineSegment(sketch, "E145.top", {"start": v(-586.32, 262.4) * mm, "end": v(-542.82, 262.4) * mm});
            skLineSegment(sketch, "E145.left", {"start": v(-586.32, 299.4) * mm, "end": v(-586.32, 292.9) * mm});
            skLineSegment(sketch, "E145.right", {"start": v(-266.32, 299.4) * mm, "end": v(-266.32, 292.9) * mm});
            skLineSegment(sketch, "E146.3.0.0", {"start": v(-542.82, 302.4) * mm, "end": v(-542.82, 299.4) * mm});
            skLineSegment(sketch, "E146.3.0.1", {"start": v(-534.82, 299.4) * mm, "end": v(-534.82, 302.4) * mm});
            skLineSegment(sketch, "E147.0.1.0", {"start": v(-542.82, 262.4) * mm, "end": v(-542.82, 259.4) * mm});
            skLineSegment(sketch, "E147.0.1.1", {"start": v(-534.82, 259.4) * mm, "end": v(-534.82, 262.4) * mm});
            skLineSegment(sketch, "E147.1.0.0", {"start": v(-467.82, 302.4) * mm, "end": v(-467.82, 299.4) * mm});
            skLineSegment(sketch, "E147.1.0.1", {"start": v(-459.82, 299.4) * mm, "end": v(-459.82, 302.4) * mm});
            skLineSegment(sketch, "E147.1.1.0", {"start": v(-467.82, 262.4) * mm, "end": v(-467.82, 259.4) * mm});
            skLineSegment(sketch, "E147.1.1.1", {"start": v(-459.82, 259.4) * mm, "end": v(-459.82, 262.4) * mm});
            skLineSegment(sketch, "E147.2.0.0", {"start": v(-392.82, 302.4) * mm, "end": v(-392.82, 299.4) * mm});
            skLineSegment(sketch, "E147.2.0.1", {"start": v(-384.82, 299.4) * mm, "end": v(-384.82, 302.4) * mm});
            skLineSegment(sketch, "E147.2.1.0", {"start": v(-392.82, 262.4) * mm, "end": v(-392.82, 259.4) * mm});
            skLineSegment(sketch, "E147.2.1.1", {"start": v(-384.82, 259.4) * mm, "end": v(-384.82, 262.4) * mm});
            skLineSegment(sketch, "E147.3.0.0", {"start": v(-317.82, 302.4) * mm, "end": v(-317.82, 299.4) * mm});
            skLineSegment(sketch, "E147.3.0.1", {"start": v(-309.82, 299.4) * mm, "end": v(-309.82, 302.4) * mm});
            skLineSegment(sketch, "E147.3.1.0", {"start": v(-317.82, 262.4) * mm, "end": v(-317.82, 259.4) * mm});
            skLineSegment(sketch, "E147.3.1.1", {"start": v(-309.82, 259.4) * mm, "end": v(-309.82, 262.4) * mm});
            skLineSegment(sketch, "E147.direction1", {"start": v(-534.82, 299.4) * mm, "end": v(-467.82, 299.4) * mm, "construction": true});
            skLineSegment(sketch, "E147.direction2", {"start": v(-542.82, 299.4) * mm, "end": v(-542.82, 259.4) * mm, "construction": true});
            skLineSegment(sketch, "E148.3.0.0", {"start": v(-655.28, 272.49) * mm, "end": v(-658.28, 272.49) * mm});
            skLineSegment(sketch, "E148.3.0.1", {"start": v(-658.28, 264.49) * mm, "end": v(-655.28, 264.49) * mm});
            skLineSegment(sketch, "E149.3.0.0", {"start": v(-263.32, 292.9) * mm, "end": v(-266.32, 292.9) * mm});
            skLineSegment(sketch, "E149.3.0.1", {"start": v(-266.32, 284.9) * mm, "end": v(-263.32, 284.9) * mm});
            skLineSegment(sketch, "E150.0.1.0", {"start": v(-263.32, 276.9) * mm, "end": v(-266.32, 276.9) * mm});
            skLineSegment(sketch, "E150.0.1.1", {"start": v(-266.32, 268.9) * mm, "end": v(-263.32, 268.9) * mm});
            skLineSegment(sketch, "E150.1.0.0", {"start": v(-586.32, 292.9) * mm, "end": v(-589.32, 292.9) * mm});
            skLineSegment(sketch, "E150.1.0.1", {"start": v(-589.32, 284.9) * mm, "end": v(-586.32, 284.9) * mm});
            skLineSegment(sketch, "E150.1.1.0", {"start": v(-586.32, 276.9) * mm, "end": v(-589.32, 276.9) * mm});
            skLineSegment(sketch, "E150.1.1.1", {"start": v(-589.32, 268.9) * mm, "end": v(-586.32, 268.9) * mm});
            skLineSegment(sketch, "E150.direction1", {"start": v(-266.32, 292.9) * mm, "end": v(-589.32, 292.9) * mm, "construction": true});
            skLineSegment(sketch, "E150.direction2", {"start": v(-266.32, 284.9) * mm, "end": v(-266.32, 276.9) * mm, "construction": true});
            skLineSegment(sketch, "E151", {"start": v(-589.32, 284.9) * mm, "end": v(-589.32, 292.9) * mm});
            skLineSegment(sketch, "E152", {"start": v(-589.32, 276.9) * mm, "end": v(-589.32, 268.9) * mm});
            skLineSegment(sketch, "E153", {"start": v(-542.82, 302.4) * mm, "end": v(-534.82, 302.4) * mm});
            skLineSegment(sketch, "E154", {"start": v(-542.82, 259.4) * mm, "end": v(-534.82, 259.4) * mm});
            skLineSegment(sketch, "E155", {"start": v(-467.82, 302.4) * mm, "end": v(-459.82, 302.4) * mm});
            skLineSegment(sketch, "E156", {"start": v(-392.82, 302.4) * mm, "end": v(-384.82, 302.4) * mm});
            skLineSegment(sketch, "E157", {"start": v(-317.82, 302.4) * mm, "end": v(-309.82, 302.4) * mm});
            skLineSegment(sketch, "E158", {"start": v(-263.32, 292.9) * mm, "end": v(-263.32, 284.9) * mm});
            skLineSegment(sketch, "E159", {"start": v(-263.32, 276.9) * mm, "end": v(-263.32, 268.9) * mm});
            skLineSegment(sketch, "E160", {"start": v(-309.82, 259.4) * mm, "end": v(-317.82, 259.4) * mm});
            skLineSegment(sketch, "E161", {"start": v(-384.82, 259.4) * mm, "end": v(-392.82, 259.4) * mm});
            skLineSegment(sketch, "E162.trimOffspring", {"start": v(-586.32, 268.9) * mm, "end": v(-586.32, 262.4) * mm});
            skLineSegment(sketch, "E163.trimOffspring", {"start": v(-586.32, 284.9) * mm, "end": v(-586.32, 276.9) * mm});
            skLineSegment(sketch, "E164.trimOffspring", {"start": v(-534.82, 299.4) * mm, "end": v(-467.82, 299.4) * mm});
            skLineSegment(sketch, "E165.trimOffspring", {"start": v(-534.82, 262.4) * mm, "end": v(-467.82, 262.4) * mm});
            skLineSegment(sketch, "E166.trimOffspring", {"start": v(-459.82, 299.4) * mm, "end": v(-392.82, 299.4) * mm});
            skLineSegment(sketch, "E167", {"start": v(-467.82, 259.4) * mm, "end": v(-459.82, 259.4) * mm});
            skLineSegment(sketch, "E168.trimOffspring", {"start": v(-459.82, 262.4) * mm, "end": v(-392.82, 262.4) * mm});
            skLineSegment(sketch, "E169.trimOffspring", {"start": v(-384.82, 262.4) * mm, "end": v(-317.82, 262.4) * mm});
            skLineSegment(sketch, "E170.trimOffspring", {"start": v(-384.82, 299.4) * mm, "end": v(-317.82, 299.4) * mm});
            skLineSegment(sketch, "E171.trimOffspring", {"start": v(-309.82, 299.4) * mm, "end": v(-266.32, 299.4) * mm});
            skLineSegment(sketch, "E172.trimOffspring", {"start": v(-309.82, 262.4) * mm, "end": v(-266.32, 262.4) * mm});
            skLineSegment(sketch, "E173.trimOffspring", {"start": v(-266.32, 268.9) * mm, "end": v(-266.32, 262.4) * mm});
            skLineSegment(sketch, "E174.trimOffspring", {"start": v(-266.32, 284.9) * mm, "end": v(-266.32, 276.9) * mm});
            skSolve(sketch);
        }
        {
            var Q0;
            Q0=makeQuery(id+"F8.imprint","IMPRINT",FACE,{"disambiguationData":[TD([[makeQuery(id+"F8.imprint","IMPRINT",EDGE,{"derivedFrom":sQuery(id+"F8.wireOp",EDGE,"E145.bottom")}),-1.0]])]});
            extrude(context, id + "F9", {"entities" : qUnion([Q0]), "depth" : 3 * mm, "offsetDistance" : 25 * mm});
        }
        {
            var Q0;
            Q0=qCreatedBy(makeId("Front.planeOp"),FACE);
            var sketch = newSketch(context, id + "F10", { "sketchPlane" : qUnion([Q0])});
            skLineSegment(sketch, "E175.bottom", {"start": v(-466.27, 223.26) * mm, "end": v(-796.27, 223.26) * mm});
            skLineSegment(sketch, "E175.left", {"start": v(-466.27, 223.26) * mm, "end": v(-466.27, 386.26) * mm});
            skLineSegment(sketch, "E175.right", {"start": v(-796.27, 223.26) * mm, "end": v(-796.27, 386.26) * mm});
            skPoint(sketch, "E176", {"position": v(-466.27, 643.26) * mm});
            skPoint(sketch, "E177", {"position": v(-796.27, 643.26) * mm});
            skArc(sketch, "E178", {"start": v(-596.27, 643.26) * mm, "mid": v(-631.27, 678.26) * mm, "end": v(-666.27, 643.26) * mm});
            skPoint(sketch, "E178.centerSnap0", {"position": v(-631.27, 223.26) * mm});
            skLineSegment(sketch, "E179.bottom", {"start": v(-468.27, 232.26) * mm, "end": v(-471.27, 232.26) * mm});
            skLineSegment(sketch, "E179.top", {"start": v(-468.27, 240.26) * mm, "end": v(-471.27, 240.26) * mm});
            skLineSegment(sketch, "E179.left", {"start": v(-468.27, 232.26) * mm, "end": v(-468.27, 240.26) * mm});
            skLineSegment(sketch, "E179.right", {"start": v(-471.27, 232.26) * mm, "end": v(-471.27, 240.26) * mm});
            skLineSegment(sketch, "E180.0.1.0", {"start": v(-468.27, 282.26) * mm, "end": v(-468.27, 290.26) * mm});
            skLineSegment(sketch, "E180.0.1.1", {"start": v(-468.27, 290.26) * mm, "end": v(-471.27, 290.26) * mm});
            skLineSegment(sketch, "E180.0.1.2", {"start": v(-471.27, 282.26) * mm, "end": v(-471.27, 290.26) * mm});
            skLineSegment(sketch, "E180.0.1.3", {"start": v(-468.27, 282.26) * mm, "end": v(-471.27, 282.26) * mm});
            skLineSegment(sketch, "E180.0.2.0", {"start": v(-468.27, 332.26) * mm, "end": v(-468.27, 340.26) * mm});
            skLineSegment(sketch, "E180.0.2.1", {"start": v(-468.27, 340.26) * mm, "end": v(-471.27, 340.26) * mm});
            skLineSegment(sketch, "E180.0.2.2", {"start": v(-471.27, 332.26) * mm, "end": v(-471.27, 340.26) * mm});
            skLineSegment(sketch, "E180.0.2.3", {"start": v(-468.27, 332.26) * mm, "end": v(-471.27, 332.26) * mm});
            skLineSegment(sketch, "E180.0.3.0", {"start": v(-468.27, 382.26) * mm, "end": v(-468.27, 386.26) * mm});
            skLineSegment(sketch, "E180.0.3.1", {"start": v(-468.27, 390.26) * mm, "end": v(-471.27, 390.26) * mm});
            skLineSegment(sketch, "E180.0.3.2", {"start": v(-471.27, 382.26) * mm, "end": v(-471.27, 386.26) * mm});
            skLineSegment(sketch, "E180.0.3.3", {"start": v(-468.27, 382.26) * mm, "end": v(-471.27, 382.26) * mm});
            skLineSegment(sketch, "E180.0.4.0", {"start": v(-468.27, 432.26) * mm, "end": v(-468.27, 440.26) * mm});
            skLineSegment(sketch, "E180.0.4.1", {"start": v(-468.27, 440.26) * mm, "end": v(-471.27, 440.26) * mm});
            skLineSegment(sketch, "E180.0.4.2", {"start": v(-471.27, 432.26) * mm, "end": v(-471.27, 440.26) * mm});
            skLineSegment(sketch, "E180.0.4.3", {"start": v(-468.27, 432.26) * mm, "end": v(-471.27, 432.26) * mm});
            skLineSegment(sketch, "E180.0.5.0", {"start": v(-468.27, 482.26) * mm, "end": v(-468.27, 490.26) * mm});
            skLineSegment(sketch, "E180.0.5.1", {"start": v(-468.27, 490.26) * mm, "end": v(-471.27, 490.26) * mm});
            skLineSegment(sketch, "E180.0.5.2", {"start": v(-471.27, 482.26) * mm, "end": v(-471.27, 490.26) * mm});
            skLineSegment(sketch, "E180.0.5.3", {"start": v(-468.27, 482.26) * mm, "end": v(-471.27, 482.26) * mm});
            skLineSegment(sketch, "E180.0.6.0", {"start": v(-468.27, 532.26) * mm, "end": v(-468.27, 540.26) * mm});
            skLineSegment(sketch, "E180.0.6.1", {"start": v(-468.27, 540.26) * mm, "end": v(-471.27, 540.26) * mm});
            skLineSegment(sketch, "E180.0.6.2", {"start": v(-471.27, 532.26) * mm, "end": v(-471.27, 540.26) * mm});
            skLineSegment(sketch, "E180.0.6.3", {"start": v(-468.27, 532.26) * mm, "end": v(-471.27, 532.26) * mm});
            skLineSegment(sketch, "E180.0.7.0", {"start": v(-468.27, 582.26) * mm, "end": v(-468.27, 590.26) * mm});
            skLineSegment(sketch, "E180.0.7.1", {"start": v(-468.27, 590.26) * mm, "end": v(-471.27, 590.26) * mm});
            skLineSegment(sketch, "E180.0.7.2", {"start": v(-471.27, 582.26) * mm, "end": v(-471.27, 590.26) * mm});
            skLineSegment(sketch, "E180.0.7.3", {"start": v(-468.27, 582.26) * mm, "end": v(-471.27, 582.26) * mm});
            skLineSegment(sketch, "E180.0.8.0", {"start": v(-468.27, 632.26) * mm, "end": v(-468.27, 640.26) * mm});
            skLineSegment(sketch, "E180.0.8.1", {"start": v(-468.27, 640.26) * mm, "end": v(-471.27, 640.26) * mm});
            skLineSegment(sketch, "E180.0.8.2", {"start": v(-471.27, 632.26) * mm, "end": v(-471.27, 640.26) * mm});
            skLineSegment(sketch, "E180.0.8.3", {"start": v(-468.27, 632.26) * mm, "end": v(-471.27, 632.26) * mm});
            skLineSegment(sketch, "E180.1.0.0", {"start": v(-791.27, 232.26) * mm, "end": v(-791.27, 240.26) * mm});
            skLineSegment(sketch, "E180.1.0.1", {"start": v(-791.27, 240.26) * mm, "end": v(-794.27, 240.26) * mm});
            skLineSegment(sketch, "E180.1.0.2", {"start": v(-794.27, 232.26) * mm, "end": v(-794.27, 240.26) * mm});
            skLineSegment(sketch, "E180.1.0.3", {"start": v(-791.27, 232.26) * mm, "end": v(-794.27, 232.26) * mm});
            skLineSegment(sketch, "E180.1.1.0", {"start": v(-791.27, 282.26) * mm, "end": v(-791.27, 290.26) * mm});
            skLineSegment(sketch, "E180.1.1.1", {"start": v(-791.27, 290.26) * mm, "end": v(-794.27, 290.26) * mm});
            skLineSegment(sketch, "E180.1.1.2", {"start": v(-794.27, 282.26) * mm, "end": v(-794.27, 290.26) * mm});
            skLineSegment(sketch, "E180.1.1.3", {"start": v(-791.27, 282.26) * mm, "end": v(-794.27, 282.26) * mm});
            skLineSegment(sketch, "E180.1.2.0", {"start": v(-791.27, 332.26) * mm, "end": v(-791.27, 340.26) * mm});
            skLineSegment(sketch, "E180.1.2.1", {"start": v(-791.27, 340.26) * mm, "end": v(-794.27, 340.26) * mm});
            skLineSegment(sketch, "E180.1.2.2", {"start": v(-794.27, 332.26) * mm, "end": v(-794.27, 340.26) * mm});
            skLineSegment(sketch, "E180.1.2.3", {"start": v(-791.27, 332.26) * mm, "end": v(-794.27, 332.26) * mm});
            skLineSegment(sketch, "E180.1.3.0", {"start": v(-791.27, 382.26) * mm, "end": v(-791.27, 386.26) * mm});
            skLineSegment(sketch, "E180.1.3.1", {"start": v(-791.27, 390.26) * mm, "end": v(-794.27, 390.26) * mm});
            skLineSegment(sketch, "E180.1.3.2", {"start": v(-794.27, 382.26) * mm, "end": v(-794.27, 386.26) * mm});
            skLineSegment(sketch, "E180.1.3.3", {"start": v(-791.27, 382.26) * mm, "end": v(-794.27, 382.26) * mm});
            skLineSegment(sketch, "E180.1.4.0", {"start": v(-791.27, 432.26) * mm, "end": v(-791.27, 440.26) * mm});
            skLineSegment(sketch, "E180.1.4.1", {"start": v(-791.27, 440.26) * mm, "end": v(-794.27, 440.26) * mm});
            skLineSegment(sketch, "E180.1.4.2", {"start": v(-794.27, 432.26) * mm, "end": v(-794.27, 440.26) * mm});
            skLineSegment(sketch, "E180.1.4.3", {"start": v(-791.27, 432.26) * mm, "end": v(-794.27, 432.26) * mm});
            skLineSegment(sketch, "E180.1.5.0", {"start": v(-791.27, 482.26) * mm, "end": v(-791.27, 490.26) * mm});
            skLineSegment(sketch, "E180.1.5.1", {"start": v(-791.27, 490.26) * mm, "end": v(-794.27, 490.26) * mm});
            skLineSegment(sketch, "E180.1.5.2", {"start": v(-794.27, 482.26) * mm, "end": v(-794.27, 490.26) * mm});
            skLineSegment(sketch, "E180.1.5.3", {"start": v(-791.27, 482.26) * mm, "end": v(-794.27, 482.26) * mm});
            skLineSegment(sketch, "E180.1.6.0", {"start": v(-791.27, 532.26) * mm, "end": v(-791.27, 540.26) * mm});
            skLineSegment(sketch, "E180.1.6.1", {"start": v(-791.27, 540.26) * mm, "end": v(-794.27, 540.26) * mm});
            skLineSegment(sketch, "E180.1.6.2", {"start": v(-794.27, 532.26) * mm, "end": v(-794.27, 540.26) * mm});
            skLineSegment(sketch, "E180.1.6.3", {"start": v(-791.27, 532.26) * mm, "end": v(-794.27, 532.26) * mm});
            skLineSegment(sketch, "E180.1.7.0", {"start": v(-791.27, 582.26) * mm, "end": v(-791.27, 590.26) * mm});
            skLineSegment(sketch, "E180.1.7.1", {"start": v(-791.27, 590.26) * mm, "end": v(-794.27, 590.26) * mm});
            skLineSegment(sketch, "E180.1.7.2", {"start": v(-794.27, 582.26) * mm, "end": v(-794.27, 590.26) * mm});
            skLineSegment(sketch, "E180.1.7.3", {"start": v(-791.27, 582.26) * mm, "end": v(-794.27, 582.26) * mm});
            skLineSegment(sketch, "E180.1.8.0", {"start": v(-791.27, 632.26) * mm, "end": v(-791.27, 640.26) * mm});
            skLineSegment(sketch, "E180.1.8.1", {"start": v(-791.27, 640.26) * mm, "end": v(-794.27, 640.26) * mm});
            skLineSegment(sketch, "E180.1.8.2", {"start": v(-794.27, 632.26) * mm, "end": v(-794.27, 640.26) * mm});
            skLineSegment(sketch, "E180.1.8.3", {"start": v(-791.27, 632.26) * mm, "end": v(-794.27, 632.26) * mm});
            skLineSegment(sketch, "E180.direction1", {"start": v(-468.27, 232.26) * mm, "end": v(-791.27, 232.26) * mm, "construction": true});
            skLineSegment(sketch, "E180.direction2", {"start": v(-468.27, 232.26) * mm, "end": v(-468.27, 282.26) * mm, "construction": true});
            skArc(sketch, "E181", {"start": v(-789.27, 643.26) * mm, "mid": v(-792.77, 646.76) * mm, "end": v(-796.27, 643.26) * mm});
            skArc(sketch, "E182", {"start": v(-466.27, 643.26) * mm, "mid": v(-469.77, 646.76) * mm, "end": v(-473.27, 643.26) * mm});
            skArc(sketch, "E183", {"start": v(-596.27, 643.26) * mm, "mid": v(-534.77, 622.11) * mm, "end": v(-473.27, 643.26) * mm});
            skArc(sketch, "E184", {"start": v(-789.27, 643.26) * mm, "mid": v(-727.77, 622.11) * mm, "end": v(-666.27, 643.26) * mm});
            skLineSegment(sketch, "E185.bottom", {"start": v(-416.33, 227.78) * mm, "end": v(-416.33, 224.78) * mm});
            skLineSegment(sketch, "E185.top", {"start": v(-424.33, 227.78) * mm, "end": v(-424.33, 224.78) * mm});
            skLineSegment(sketch, "E185.left", {"start": v(-416.33, 227.78) * mm, "end": v(-424.33, 227.78) * mm});
            skLineSegment(sketch, "E185.right", {"start": v(-416.33, 224.78) * mm, "end": v(-424.33, 224.78) * mm});
            skLineSegment(sketch, "E186.bottom", {"start": v(-514.77, 386.26) * mm, "end": v(-514.77, 383.26) * mm});
            skLineSegment(sketch, "E186.top", {"start": v(-522.77, 386.26) * mm, "end": v(-522.77, 383.26) * mm});
            skLineSegment(sketch, "E186.right", {"start": v(-514.77, 383.26) * mm, "end": v(-522.77, 383.26) * mm});
            skLineSegment(sketch, "E187.0.1.0", {"start": v(-514.77, 539.26) * mm, "end": v(-522.77, 539.26) * mm});
            skLineSegment(sketch, "E187.0.1.1", {"start": v(-514.77, 536.26) * mm, "end": v(-522.77, 536.26) * mm});
            skLineSegment(sketch, "E187.0.1.2", {"start": v(-522.77, 539.26) * mm, "end": v(-522.77, 536.26) * mm});
            skLineSegment(sketch, "E187.0.1.3", {"start": v(-514.77, 539.26) * mm, "end": v(-514.77, 536.26) * mm});
            skLineSegment(sketch, "E187.1.0.1", {"start": v(-589.77, 383.26) * mm, "end": v(-597.77, 383.26) * mm});
            skLineSegment(sketch, "E187.1.0.2", {"start": v(-597.77, 386.26) * mm, "end": v(-597.77, 383.26) * mm});
            skLineSegment(sketch, "E187.1.0.3", {"start": v(-589.77, 386.26) * mm, "end": v(-589.77, 383.26) * mm});
            skLineSegment(sketch, "E187.1.1.0", {"start": v(-589.77, 539.26) * mm, "end": v(-597.77, 539.26) * mm});
            skLineSegment(sketch, "E187.1.1.1", {"start": v(-589.77, 536.26) * mm, "end": v(-597.77, 536.26) * mm});
            skLineSegment(sketch, "E187.1.1.2", {"start": v(-597.77, 539.26) * mm, "end": v(-597.77, 536.26) * mm});
            skLineSegment(sketch, "E187.1.1.3", {"start": v(-589.77, 539.26) * mm, "end": v(-589.77, 536.26) * mm});
            skLineSegment(sketch, "E187.2.0.1", {"start": v(-664.77, 383.26) * mm, "end": v(-672.77, 383.26) * mm});
            skLineSegment(sketch, "E187.2.0.2", {"start": v(-672.77, 386.26) * mm, "end": v(-672.77, 383.26) * mm});
            skLineSegment(sketch, "E187.2.0.3", {"start": v(-664.77, 386.26) * mm, "end": v(-664.77, 383.26) * mm});
            skLineSegment(sketch, "E187.2.1.0", {"start": v(-664.77, 539.26) * mm, "end": v(-672.77, 539.26) * mm});
            skLineSegment(sketch, "E187.2.1.1", {"start": v(-664.77, 536.26) * mm, "end": v(-672.77, 536.26) * mm});
            skLineSegment(sketch, "E187.2.1.2", {"start": v(-672.77, 539.26) * mm, "end": v(-672.77, 536.26) * mm});
            skLineSegment(sketch, "E187.2.1.3", {"start": v(-664.77, 539.26) * mm, "end": v(-664.77, 536.26) * mm});
            skLineSegment(sketch, "E187.3.0.1", {"start": v(-739.77, 383.26) * mm, "end": v(-747.77, 383.26) * mm});
            skLineSegment(sketch, "E187.3.0.2", {"start": v(-747.77, 386.26) * mm, "end": v(-747.77, 383.26) * mm});
            skLineSegment(sketch, "E187.3.0.3", {"start": v(-739.77, 386.26) * mm, "end": v(-739.77, 383.26) * mm});
            skLineSegment(sketch, "E187.3.1.0", {"start": v(-739.77, 539.26) * mm, "end": v(-747.77, 539.26) * mm});
            skLineSegment(sketch, "E187.3.1.1", {"start": v(-739.77, 536.26) * mm, "end": v(-747.77, 536.26) * mm});
            skLineSegment(sketch, "E187.3.1.2", {"start": v(-747.77, 539.26) * mm, "end": v(-747.77, 536.26) * mm});
            skLineSegment(sketch, "E187.3.1.3", {"start": v(-739.77, 539.26) * mm, "end": v(-739.77, 536.26) * mm});
            skLineSegment(sketch, "E187.direction1", {"start": v(-522.77, 386.26) * mm, "end": v(-589.77, 386.26) * mm, "construction": true});
            skLineSegment(sketch, "E187.direction2", {"start": v(-522.77, 386.26) * mm, "end": v(-522.77, 539.26) * mm, "construction": true});
            skLineSegment(sketch, "E188", {"start": v(-471.27, 386.26) * mm, "end": v(-514.77, 386.26) * mm});
            skLineSegment(sketch, "E189", {"start": v(-468.27, 386.26) * mm, "end": v(-466.27, 386.26) * mm});
            skLineSegment(sketch, "E190", {"start": v(-522.77, 386.26) * mm, "end": v(-589.77, 386.26) * mm});
            skLineSegment(sketch, "E191", {"start": v(-597.77, 386.26) * mm, "end": v(-664.77, 386.26) * mm});
            skLineSegment(sketch, "E192", {"start": v(-672.77, 386.26) * mm, "end": v(-739.77, 386.26) * mm});
            skLineSegment(sketch, "E193", {"start": v(-747.77, 386.26) * mm, "end": v(-791.27, 386.26) * mm});
            skLineSegment(sketch, "E194", {"start": v(-794.27, 386.26) * mm, "end": v(-796.27, 386.26) * mm});
            skLineSegment(sketch, "E195", {"start": v(-466.27, 386.46) * mm, "end": v(-468.27, 386.46) * mm});
            skLineSegment(sketch, "E196", {"start": v(-471.27, 386.46) * mm, "end": v(-791.27, 386.46) * mm});
            skLineSegment(sketch, "E197", {"start": v(-794.27, 386.46) * mm, "end": v(-796.27, 386.46) * mm});
            skLineSegment(sketch, "E198.trimOffspring", {"start": v(-791.27, 386.46) * mm, "end": v(-791.27, 390.26) * mm});
            skLineSegment(sketch, "E199.trimOffspring", {"start": v(-794.27, 386.46) * mm, "end": v(-794.27, 390.26) * mm});
            skLineSegment(sketch, "E200.trimOffspring", {"start": v(-796.27, 386.46) * mm, "end": v(-796.27, 643.26) * mm});
            skLineSegment(sketch, "E201.trimOffspring", {"start": v(-466.27, 386.46) * mm, "end": v(-466.27, 643.26) * mm});
            skLineSegment(sketch, "E202.trimOffspring", {"start": v(-468.27, 386.46) * mm, "end": v(-468.27, 390.26) * mm});
            skLineSegment(sketch, "E203.trimOffspring", {"start": v(-471.27, 386.46) * mm, "end": v(-471.27, 390.26) * mm});
            skSolve(sketch);
        }
        {
            var Q0;
            Q0=qCreatedBy(makeId("Front.planeOp"),FACE);
            var sketch = newSketch(context, id + "F11", { "sketchPlane" : qUnion([Q0])});
            skLineSegment(sketch, "E204.bottom", {"start": v(120.76, 22.93) * mm, "end": v(128.76, 22.93) * mm});
            skLineSegment(sketch, "E204.top", {"start": v(120.76, 17.93) * mm, "end": v(128.76, 17.93) * mm});
            skLineSegment(sketch, "E204.left", {"start": v(120.76, 22.93) * mm, "end": v(120.76, 17.93) * mm});
            skLineSegment(sketch, "E204.right", {"start": v(128.76, 22.93) * mm, "end": v(128.76, 19.93) * mm});
            skLineSegment(sketch, "E205.1.0.0", {"start": v(195.76, 22.93) * mm, "end": v(203.76, 22.93) * mm});
            skLineSegment(sketch, "E205.1.0.1", {"start": v(195.76, 22.93) * mm, "end": v(195.76, 19.93) * mm});
            skLineSegment(sketch, "E205.1.0.2", {"start": v(203.76, 22.93) * mm, "end": v(203.76, 19.93) * mm});
            skLineSegment(sketch, "E205.1.0.3", {"start": v(195.76, 17.93) * mm, "end": v(203.76, 17.93) * mm});
            skLineSegment(sketch, "E205.2.0.0", {"start": v(270.76, 22.93) * mm, "end": v(278.76, 22.93) * mm});
            skLineSegment(sketch, "E205.2.0.1", {"start": v(270.76, 22.93) * mm, "end": v(270.76, 19.93) * mm});
            skLineSegment(sketch, "E205.2.0.2", {"start": v(278.76, 22.93) * mm, "end": v(278.76, 19.93) * mm});
            skLineSegment(sketch, "E205.2.0.3", {"start": v(270.76, 17.93) * mm, "end": v(278.76, 17.93) * mm});
            skLineSegment(sketch, "E205.3.0.0", {"start": v(345.76, 22.93) * mm, "end": v(353.76, 22.93) * mm});
            skLineSegment(sketch, "E205.3.0.1", {"start": v(345.76, 22.93) * mm, "end": v(345.76, 19.93) * mm});
            skLineSegment(sketch, "E205.3.0.2", {"start": v(353.76, 22.93) * mm, "end": v(353.76, 17.93) * mm});
            skLineSegment(sketch, "E205.3.0.3", {"start": v(345.76, 17.93) * mm, "end": v(353.76, 17.93) * mm});
            skLineSegment(sketch, "E205.direction1", {"start": v(120.76, 22.93) * mm, "end": v(195.76, 22.93) * mm, "construction": true});
            skLineSegment(sketch, "E206", {"start": v(128.76, 17.93) * mm, "end": v(195.76, 17.93) * mm});
            skLineSegment(sketch, "E207", {"start": v(203.76, 17.93) * mm, "end": v(270.76, 17.93) * mm});
            skLineSegment(sketch, "E208", {"start": v(278.76, 17.93) * mm, "end": v(345.76, 17.93) * mm});
            skLineSegment(sketch, "E209", {"start": v(345.76, 19.93) * mm, "end": v(278.76, 19.93) * mm});
            skLineSegment(sketch, "E210.trimOffspring", {"start": v(195.76, 19.93) * mm, "end": v(128.76, 19.93) * mm});
            skLineSegment(sketch, "E211.trimOffspring", {"start": v(270.76, 19.93) * mm, "end": v(203.76, 19.93) * mm});
            skSolve(sketch);
        }
        {
            var Q0;
            Q0=makeQuery(id+"F10.imprint","IMPRINT",FACE,{"disambiguationData":[TD([[makeQuery(id+"F10.imprint","IMPRINT",EDGE,{"derivedFrom":sQuery(id+"F10.wireOp",EDGE,"E175.bottom")}),-1.0]])]});
            extrude(context, id + "F12", {"entities" : qUnion([Q0]), "depth" : 3 * mm, "offsetDistance" : 25 * mm});
        }
        {
            var Q0;
            Q0=makeQuery(id+"F10.imprint","IMPRINT",FACE,{"disambiguationData":[TD([[makeQuery(id+"F10.imprint","IMPRINT",EDGE,{"derivedFrom":sQuery(id+"F10.wireOp",EDGE,"E178")}),1.0]])]});
            extrude(context, id + "F13", {"entities" : qUnion([Q0]), "operationType" : NewBodyOperationType.ADD, "depth" : 3 * mm, "offsetDistance" : 25 * mm});
        }
        {
            var Q0;
            Q0=makeQuery(id+"F11.imprint","IMPRINT",FACE,{"disambiguationData":[TD([[makeQuery(id+"F11.imprint","IMPRINT",EDGE,{"derivedFrom":sQuery(id+"F11.wireOp",EDGE,"E204.bottom")}),-1.0]])]});
            extrude(context, id + "F14", {"entities" : qUnion([Q0]), "depth" : 3 * mm, "offsetDistance" : 25 * mm});
        }
        {
            var Q0;
            Q0=qCreatedBy(makeId("Top.planeOp"),FACE);
            var sketch = newSketch(context, id + "F15", { "sketchPlane" : qUnion([Q0])});
            skCircle(sketch, "E212", {"center": v(-117.77, 114.16) * mm, "radius": 21.5 * mm});
            skCircle(sketch, "E213", {"center": v(-47.38, 138.17) * mm, "radius": 21.5 * mm});
            skSolve(sketch);
        }
        {
            var Q0;
            Q0=makeQuery(id+"F15.imprint","IMPRINT",FACE,{"disambiguationData":[TD([[makeQuery(id+"F15.imprint","IMPRINT",EDGE,{"derivedFrom":sQuery(id+"F15.wireOp",EDGE,"E212")}),1.0]])]});
            extrude(context, id + "F16", {"entities" : qUnion([Q0]), "depth" : 130 * mm, "offsetDistance" : 25 * mm});
        }
        {
            var Q0;
            Q0=makeQuery(id+"F15.imprint","IMPRINT",FACE,{"disambiguationData":[TD([[makeQuery(id+"F15.imprint","IMPRINT",EDGE,{"derivedFrom":sQuery(id+"F15.wireOp",EDGE,"E213")}),1.0]])]});
            extrude(context, id + "F17", {"entities" : qUnion([Q0]), "depth" : 117 * mm, "offsetDistance" : 25 * mm});
        }
    });
